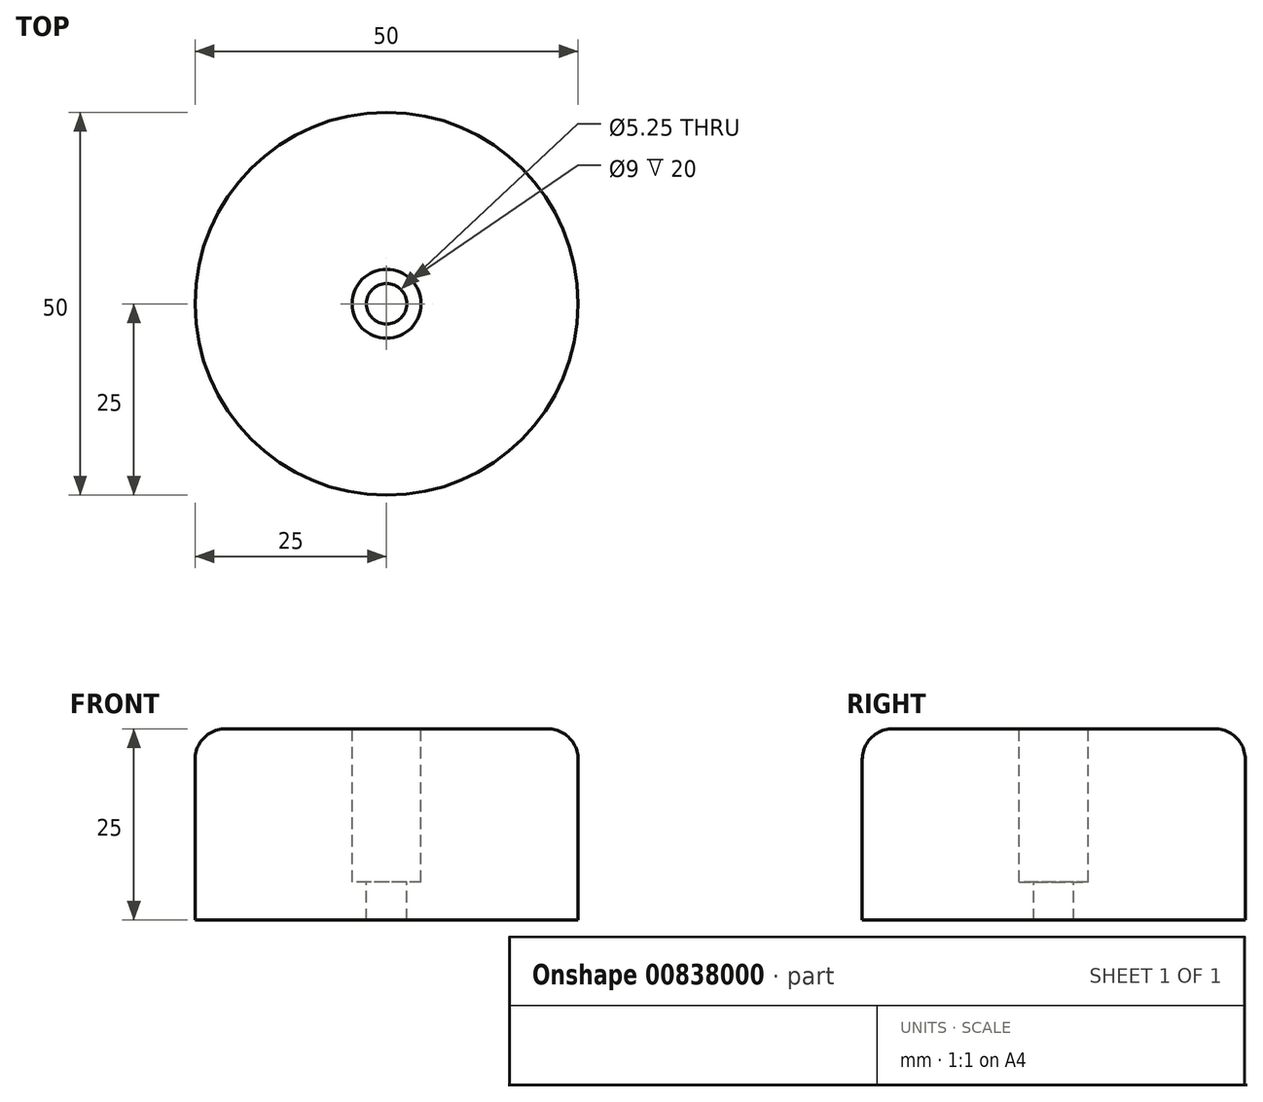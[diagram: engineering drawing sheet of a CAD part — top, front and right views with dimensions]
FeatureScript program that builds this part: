
annotation { "Feature Type Name" : "Feature", "Feature Type Description" : "" }
export const myFeature = defineFeature(function(context is Context, id is Id, definition is map)
    precondition{}
    {
        {
            var Q0;
            Q0=qCreatedBy(makeId("Top.planeOp"),FACE);
            var sketch = newSketch(context, id + "F0", { "sketchPlane" : qUnion([Q0])});
            skCircle(sketch, "E0", {"center": v(0, 0) * mm, "radius": 25 * mm});
            skSolve(sketch);
        }
        {
            var Q0;
            Q0 = qSketchRegion(id + "F0", true);
            extrude(context, id + "F1", {"entities" : qUnion([Q0]), "depth" : 25 * mm, "offsetDistance" : 25 * mm});
        }
        {
            var Q0;
            Q0=makeQuery(id+"F1.opExtrude","CAP_FACE",FACE,{"disambiguationData":[OSD([sQuery(id+"F0.wireOp",EDGE,"E0")])],"isStart":false});
            var sketch = newSketch(context, id + "F2", { "sketchPlane" : qUnion([Q0])});
            skCircle(sketch, "E1", {"center": v(0, 0) * mm, "radius": 2.62 * mm});
            skSolve(sketch);
        }
        {
            var Q0;
            Q0 = qSketchRegion(id + "F2", true);
            extrude(context, id + "F3", {"entities" : qUnion([Q0]), "operationType" : NewBodyOperationType.REMOVE, "oppositeDirection" : true, "depth" : 25 * mm, "offsetDistance" : 25 * mm});
        }
        {
            var Q0;
            Q0=makeQuery(id+"F1.opExtrude","CAP_FACE",FACE,{"disambiguationData":[OSD([sQuery(id+"F0.wireOp",EDGE,"E0")])],"isStart":false});
            var sketch = newSketch(context, id + "F4", { "sketchPlane" : qUnion([Q0])});
            skCircle(sketch, "E2", {"center": v(0, 0) * mm, "radius": 4.5 * mm});
            skSolve(sketch);
        }
        {
            var Q0;
            Q0 = qSketchRegion(id + "F4", true);
            extrude(context, id + "F5", {"entities" : qUnion([Q0]), "operationType" : NewBodyOperationType.REMOVE, "oppositeDirection" : true, "depth" : 20 * mm, "offsetDistance" : 25 * mm});
        }
        {
            var Q0;
            Q0=makeQuery(id+"F1.opExtrude","CAP_EDGE",EDGE,{"disambiguationData":[OSD([sQuery(id+"F0.wireOp",EDGE,"E0")])],"isStart":false});
            fillet(context, id + "F6", {"entities" : qUnion([Q0]), "radius" : 4 * mm, "tangentPropagation" : true, "allowEdgeOverflow" : false});
        }
    });
